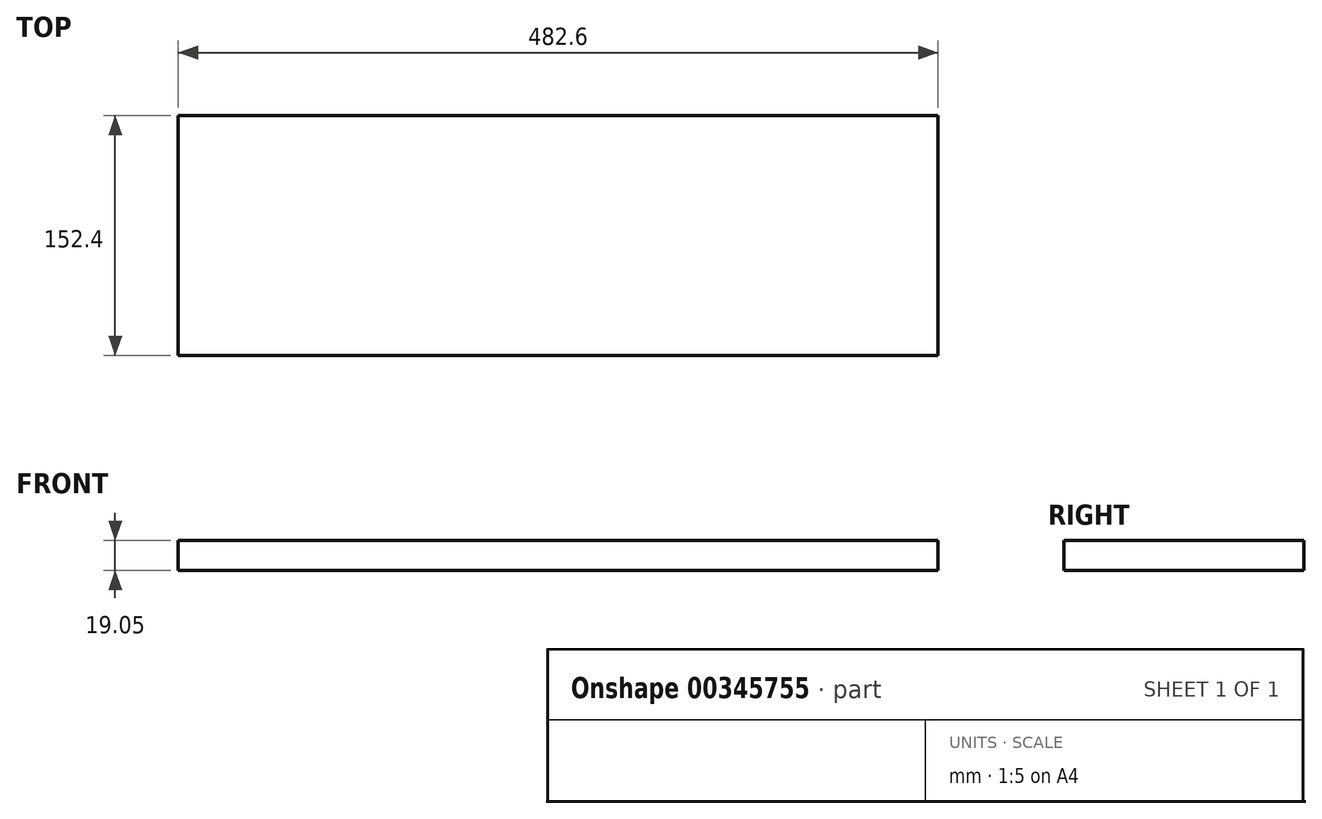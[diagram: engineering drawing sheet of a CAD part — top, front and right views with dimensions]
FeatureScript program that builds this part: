
annotation { "Feature Type Name" : "Feature", "Feature Type Description" : "" }
export const myFeature = defineFeature(function(context is Context, id is Id, definition is map)
    precondition{}
    {
        {
            var Q0;
            Q0=qCreatedBy(makeId("Top.planeOp"),FACE);
            var sketch = newSketch(context, id + "F0", { "sketchPlane" : qUnion([Q0])});
            skLineSegment(sketch, "E0.bottom", {"start": v(241.3, 76.2) * mm, "end": v(-241.3, 76.2) * mm});
            skLineSegment(sketch, "E0.top", {"start": v(241.3, -76.2) * mm, "end": v(-241.3, -76.2) * mm});
            skLineSegment(sketch, "E0.left", {"start": v(241.3, 76.2) * mm, "end": v(241.3, -76.2) * mm});
            skLineSegment(sketch, "E0.right", {"start": v(-241.3, 76.2) * mm, "end": v(-241.3, -76.2) * mm});
            skPoint(sketch, "E0.middle", {"position": v(0, 0) * mm});
            skSolve(sketch);
        }
        {
            var Q0;
            Q0 = qSketchRegion(id + "F0", true);
            extrude(context, id + "F1", {"entities" : qUnion([Q0]), "oppositeDirection" : true, "depth" : 19.05 * mm});
        }
        {
            var Q0;
            Q0=makeQuery(id+"F1.opExtrude","SWEPT_FACE",FACE,{"disambiguationData":[OSD([sQuery(id+"F0.wireOp",EDGE,"E0.left")])]});
            cPlane(context, id + "F2", {"entities" : qUnion([Q0]), "cplaneType" : CPlaneType.OFFSET, "offset" : 0 * mm, "width" : 152.4 * mm, "height" : 152.4 * mm});
        }
    });
